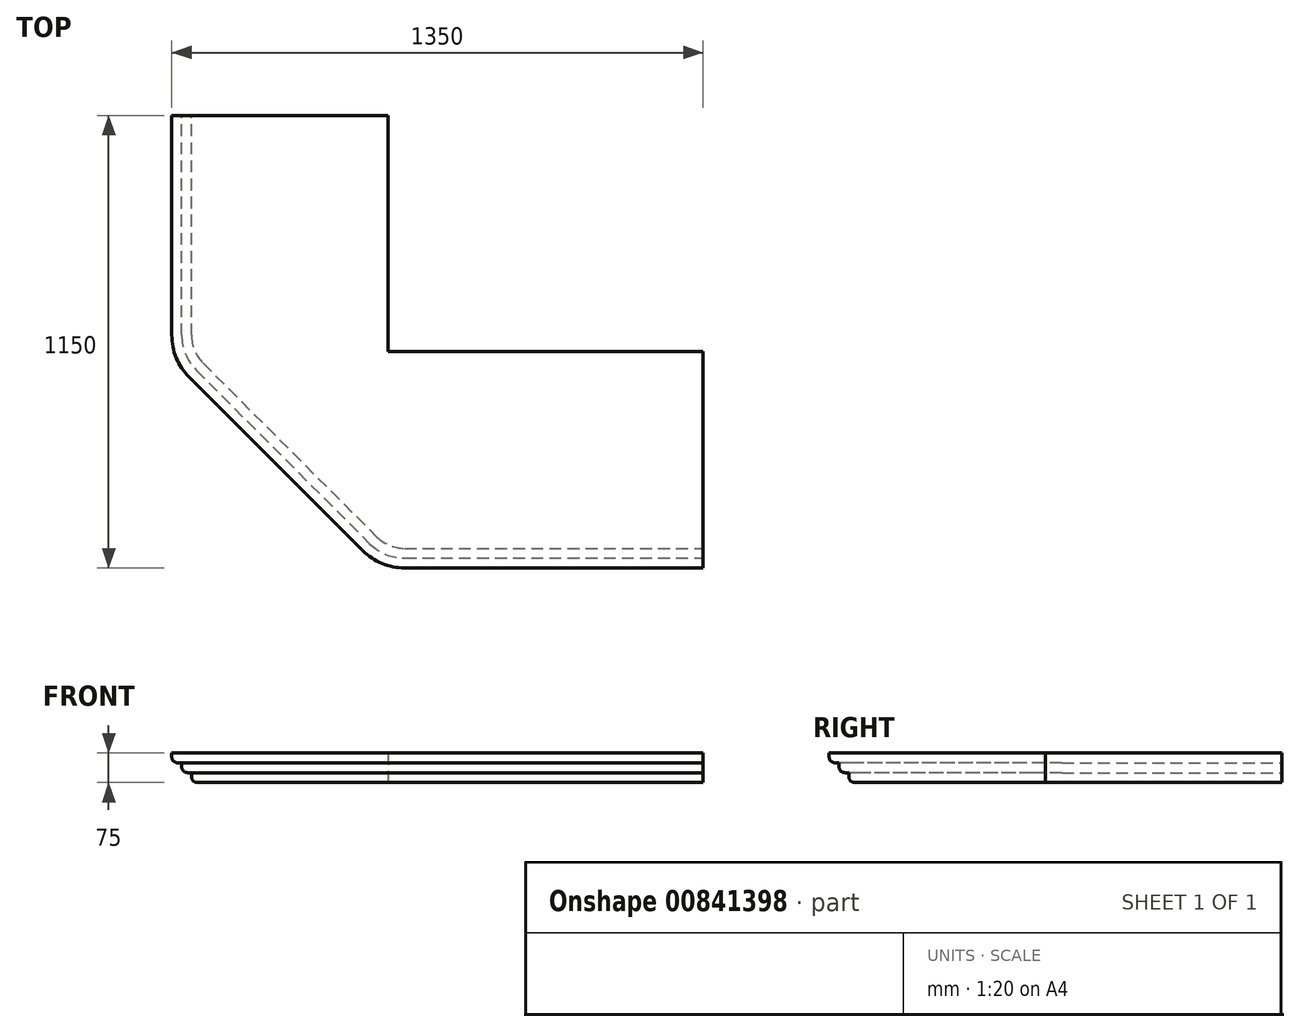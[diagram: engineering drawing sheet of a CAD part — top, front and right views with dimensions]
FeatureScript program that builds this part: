
annotation { "Feature Type Name" : "Feature", "Feature Type Description" : "" }
export const myFeature = defineFeature(function(context is Context, id is Id, definition is map)
    precondition{}
    {
        {
            var Q0;
            Q0=qCreatedBy(makeId("Top.planeOp"),FACE);
            var sketch = newSketch(context, id + "F0", { "sketchPlane" : qUnion([Q0])});
            skLineSegment(sketch, "E0.top", {"start": v(0, 600) * mm, "end": v(-500, 600) * mm});
            skLineSegment(sketch, "E0.left", {"start": v(0, 0) * mm, "end": v(0, 600) * mm});
            skLineSegment(sketch, "E0.right", {"start": v(-500, 0) * mm, "end": v(-500, 600) * mm});
            skLineSegment(sketch, "E1.bottom", {"start": v(0, 0) * mm, "end": v(800, 0) * mm});
            skLineSegment(sketch, "E1.top", {"start": v(0, -500) * mm, "end": v(800, -500) * mm});
            skLineSegment(sketch, "E1.right", {"start": v(800, 0) * mm, "end": v(800, -500) * mm});
            skLineSegment(sketch, "E2", {"start": v(-500, 0) * mm, "end": v(0, -500) * mm});
            skSolve(sketch);
        }
        {
            var Q0;
            Q0 = qSketchRegion(id + "F0", true);
            extrude(context, id + "F1", {"entities" : qUnion([Q0]), "depth" : 25 * mm, "offsetDistance" : 25 * mm});
        }
        {
            var Q0;
            Q0=makeQuery(id+"F1.opExtrude","SWEPT_EDGE",EDGE,{"disambiguationData":[OSD([sQuery(id+"F0.wireOp",EDGE,"E0.right"),sQuery(id+"F0.wireOp",EDGE,"E2")])]});
            var Q1;
            Q1=makeQuery(id+"F1.opExtrude","SWEPT_EDGE",EDGE,{"disambiguationData":[OSD([sQuery(id+"F0.wireOp",EDGE,"E1.top"),sQuery(id+"F0.wireOp",EDGE,"E2")])]});
            fillet(context, id + "F2", {"entities" : qUnion([Q0, Q1]), "radius" : 100 * mm, "tangentPropagation" : true, "allowEdgeOverflow" : false});
        }
        {
            var Q0;
            Q0=makeQuery(id+"F1.opExtrude","CAP_FACE",FACE,{"disambiguationData":[OSD([sQuery(id+"F0.wireOp",EDGE,"E0.top"),sQuery(id+"F0.wireOp",EDGE,"E0.left"),sQuery(id+"F0.wireOp",EDGE,"E0.right"),sQuery(id+"F0.wireOp",EDGE,"E1.bottom"),sQuery(id+"F0.wireOp",EDGE,"E1.top"),sQuery(id+"F0.wireOp",EDGE,"E1.right"),sQuery(id+"F0.wireOp",EDGE,"E2")])],"isStart":false});
            var sketch = newSketch(context, id + "F3", { "sketchPlane" : qUnion([Q0])});
            skArc(sketch, "E3.0", {"start": v(-525, 41.42) * mm, "mid": v(-515.48, -6.41) * mm, "end": v(-488.39, -46.97) * mm});
            skLineSegment(sketch, "E3.1", {"start": v(-488.39, -46.97) * mm, "end": v(-46.97, -488.39) * mm});
            skLineSegment(sketch, "E3.2", {"start": v(-525, 41.42) * mm, "end": v(-525, 625) * mm});
            skArc(sketch, "E3.3", {"start": v(-46.97, -488.39) * mm, "mid": v(-6.41, -515.48) * mm, "end": v(41.42, -525) * mm});
            skLineSegment(sketch, "E3.4", {"start": v(41.42, -525) * mm, "end": v(825, -525) * mm});
            skLineSegment(sketch, "E3.5", {"start": v(25, 625) * mm, "end": v(-525, 625) * mm});
            skLineSegment(sketch, "E3.6", {"start": v(25, 25) * mm, "end": v(25, 625) * mm});
            skLineSegment(sketch, "E3.7", {"start": v(25, 25) * mm, "end": v(825, 25) * mm});
            skLineSegment(sketch, "E3.8", {"start": v(825, 25) * mm, "end": v(825, -525) * mm});
            skSolve(sketch);
        }
        {
            var Q0;
            Q0 = qSketchRegion(id + "F3", true);
            extrude(context, id + "F4", {"entities" : qUnion([Q0]), "operationType" : NewBodyOperationType.ADD, "depth" : 25 * mm, "offsetDistance" : 25 * mm});
        }
        {
            var Q0;
            Q0=makeQuery(id+"F4.opExtrude","CAP_FACE",FACE,{"disambiguationData":[OSD([sQuery(id+"F3.wireOp",EDGE,"E3.0"),sQuery(id+"F3.wireOp",EDGE,"E3.1"),sQuery(id+"F3.wireOp",EDGE,"E3.2"),sQuery(id+"F3.wireOp",EDGE,"E3.3"),sQuery(id+"F3.wireOp",EDGE,"E3.4"),sQuery(id+"F3.wireOp",EDGE,"E3.5"),sQuery(id+"F3.wireOp",EDGE,"E3.6"),sQuery(id+"F3.wireOp",EDGE,"E3.7"),sQuery(id+"F3.wireOp",EDGE,"E3.8")])],"isStart":false});
            var sketch = newSketch(context, id + "F5", { "sketchPlane" : qUnion([Q0])});
            skArc(sketch, "E4.0", {"start": v(-550, 41.42) * mm, "mid": v(-538.58, -15.98) * mm, "end": v(-506.07, -64.64) * mm});
            skLineSegment(sketch, "E4.1", {"start": v(-506.07, -64.64) * mm, "end": v(-64.64, -506.07) * mm});
            skLineSegment(sketch, "E4.2", {"start": v(-550, 41.42) * mm, "end": v(-550, 650) * mm});
            skArc(sketch, "E4.3", {"start": v(-64.64, -506.07) * mm, "mid": v(-15.98, -538.58) * mm, "end": v(41.42, -550) * mm});
            skLineSegment(sketch, "E4.4", {"start": v(41.42, -550) * mm, "end": v(850, -550) * mm});
            skLineSegment(sketch, "E4.5", {"start": v(50, 650) * mm, "end": v(-550, 650) * mm});
            skLineSegment(sketch, "E4.6", {"start": v(50, 50) * mm, "end": v(50, 650) * mm});
            skLineSegment(sketch, "E4.7", {"start": v(50, 50) * mm, "end": v(850, 50) * mm});
            skLineSegment(sketch, "E4.8", {"start": v(850, 50) * mm, "end": v(850, -550) * mm});
            skSolve(sketch);
        }
        {
            var Q0;
            Q0 = qSketchRegion(id + "F5", true);
            extrude(context, id + "F6", {"entities" : qUnion([Q0]), "operationType" : NewBodyOperationType.ADD, "depth" : 25 * mm, "offsetDistance" : 25 * mm});
        }
        {
            var Q0;
            Q0=makeQuery(id+"F1.opExtrude","CAP_FACE",FACE,{"disambiguationData":[OSD([sQuery(id+"F0.wireOp",EDGE,"E0.top"),sQuery(id+"F0.wireOp",EDGE,"E0.left"),sQuery(id+"F0.wireOp",EDGE,"E0.right"),sQuery(id+"F0.wireOp",EDGE,"E1.bottom"),sQuery(id+"F0.wireOp",EDGE,"E1.top"),sQuery(id+"F0.wireOp",EDGE,"E1.right"),sQuery(id+"F0.wireOp",EDGE,"E2")])],"isStart":true});
            var sketch = newSketch(context, id + "F7", { "sketchPlane" : qUnion([Q0])});
            skLineSegment(sketch, "E5", {"start": v(800, 0) * mm, "end": v(800, 0) * mm});
            skLineSegment(sketch, "E6", {"start": v(800, 0) * mm, "end": v(0, 0) * mm});
            skLineSegment(sketch, "E7", {"start": v(0, 0) * mm, "end": v(0, -600) * mm});
            skLineSegment(sketch, "E8", {"start": v(0, -600) * mm, "end": v(-650.83, -600) * mm});
            skLineSegment(sketch, "E9", {"start": v(-650.83, -600) * mm, "end": v(-650.83, -840.36) * mm});
            skLineSegment(sketch, "E10", {"start": v(-650.83, -840.36) * mm, "end": v(869.27, -840.36) * mm});
            skLineSegment(sketch, "E11", {"start": v(869.27, -840.36) * mm, "end": v(869.27, 0) * mm});
            skLineSegment(sketch, "E12", {"start": v(800, 0) * mm, "end": v(800, 759.88) * mm});
            skLineSegment(sketch, "E13", {"start": v(800, 759.88) * mm, "end": v(869.27, 759.88) * mm});
            skLineSegment(sketch, "E14", {"start": v(869.27, 759.88) * mm, "end": v(869.27, 0) * mm});
            skSolve(sketch);
        }
        {
            var Q0;
            Q0 = qSketchRegion(id + "F7", true);
            extrude(context, id + "F8", {"entities" : qUnion([Q0]), "operationType" : NewBodyOperationType.REMOVE, "oppositeDirection" : true, "depth" : 539 * mm, "offsetDistance" : 25 * mm});
        }
        {
            var Q0;
            Q0=makeQuery(id+"F1.opExtrude","CAP_EDGE",EDGE,{"disambiguationData":[OSD([sQuery(id+"F0.wireOp",EDGE,"E1.top")])],"isStart":true});
            var Q1;
            Q1=makeQuery(id+"F4.opExtrude","CAP_EDGE",EDGE,{"disambiguationData":[OSD([sQuery(id+"F3.wireOp",EDGE,"E3.4")])],"isStart":true});
            var Q2;
            Q2=makeQuery(id+"F6.opExtrude","CAP_EDGE",EDGE,{"disambiguationData":[OSD([sQuery(id+"F5.wireOp",EDGE,"E4.4")])],"isStart":true});
            var Q3;
            {var subQ0=sQuery(id+"F0.wireOp",EDGE,"E2");var subQ1=sQuery(id+"F0.wireOp",EDGE,"E1.top");Q3=makeQuery(id+"F2.opFillet","BLEND_EDGE",EDGE,{"blendedFrom":[makeQuery(id+"F1.opExtrude","SWEPT_EDGE",EDGE,{"disambiguationData":[OSD([subQ1,subQ0])]}),makeQuery(id+"F1.opExtrude","CAP_FACE",FACE,{"disambiguationData":[OSD([sQuery(id+"F0.wireOp",EDGE,"E0.top"),sQuery(id+"F0.wireOp",EDGE,"E0.left"),sQuery(id+"F0.wireOp",EDGE,"E0.right"),sQuery(id+"F0.wireOp",EDGE,"E1.bottom"),subQ1,sQuery(id+"F0.wireOp",EDGE,"E1.right"),subQ0])],"isStart":true})],"blendedInto":[makeQuery(id+"F1.opExtrude","CAP_FACE",FACE,{"disambiguationData":[OSD([sQuery(id+"F0.wireOp",EDGE,"E0.top"),sQuery(id+"F0.wireOp",EDGE,"E0.left"),sQuery(id+"F0.wireOp",EDGE,"E0.right"),sQuery(id+"F0.wireOp",EDGE,"E1.bottom"),subQ1,sQuery(id+"F0.wireOp",EDGE,"E1.right"),subQ0])],"isStart":true})]});}
            var Q4;
            Q4=makeQuery(id+"F4.opExtrude","CAP_EDGE",EDGE,{"disambiguationData":[OSD([sQuery(id+"F3.wireOp",EDGE,"E3.3")])],"isStart":true});
            var Q5;
            Q5=makeQuery(id+"F6.opExtrude","CAP_EDGE",EDGE,{"disambiguationData":[OSD([sQuery(id+"F5.wireOp",EDGE,"E4.3")])],"isStart":true});
            var Q6;
            Q6=makeQuery(id+"F1.opExtrude","CAP_EDGE",EDGE,{"disambiguationData":[OSD([sQuery(id+"F0.wireOp",EDGE,"E2")])],"isStart":true});
            var Q7;
            Q7=makeQuery(id+"F4.opExtrude","CAP_EDGE",EDGE,{"disambiguationData":[OSD([sQuery(id+"F3.wireOp",EDGE,"E3.1")])],"isStart":true});
            var Q8;
            Q8=makeQuery(id+"F6.opExtrude","CAP_EDGE",EDGE,{"disambiguationData":[OSD([sQuery(id+"F5.wireOp",EDGE,"E4.1")])],"isStart":true});
            var Q9;
            {var subQ0=sQuery(id+"F0.wireOp",EDGE,"E2");var subQ1=sQuery(id+"F0.wireOp",EDGE,"E0.right");Q9=makeQuery(id+"F2.opFillet","BLEND_EDGE",EDGE,{"blendedFrom":[makeQuery(id+"F1.opExtrude","SWEPT_EDGE",EDGE,{"disambiguationData":[OSD([subQ1,subQ0])]}),makeQuery(id+"F1.opExtrude","CAP_FACE",FACE,{"disambiguationData":[OSD([sQuery(id+"F0.wireOp",EDGE,"E0.top"),sQuery(id+"F0.wireOp",EDGE,"E0.left"),subQ1,sQuery(id+"F0.wireOp",EDGE,"E1.bottom"),sQuery(id+"F0.wireOp",EDGE,"E1.top"),sQuery(id+"F0.wireOp",EDGE,"E1.right"),subQ0])],"isStart":true})],"blendedInto":[makeQuery(id+"F1.opExtrude","CAP_FACE",FACE,{"disambiguationData":[OSD([sQuery(id+"F0.wireOp",EDGE,"E0.top"),sQuery(id+"F0.wireOp",EDGE,"E0.left"),subQ1,sQuery(id+"F0.wireOp",EDGE,"E1.bottom"),sQuery(id+"F0.wireOp",EDGE,"E1.top"),sQuery(id+"F0.wireOp",EDGE,"E1.right"),subQ0])],"isStart":true})]});}
            var Q10;
            Q10=makeQuery(id+"F4.opExtrude","CAP_EDGE",EDGE,{"disambiguationData":[OSD([sQuery(id+"F3.wireOp",EDGE,"E3.0")])],"isStart":true});
            var Q11;
            Q11=makeQuery(id+"F6.opExtrude","CAP_EDGE",EDGE,{"disambiguationData":[OSD([sQuery(id+"F5.wireOp",EDGE,"E4.0")])],"isStart":true});
            var Q12;
            Q12=makeQuery(id+"F1.opExtrude","CAP_EDGE",EDGE,{"disambiguationData":[OSD([sQuery(id+"F0.wireOp",EDGE,"E0.right")])],"isStart":true});
            var Q13;
            Q13=makeQuery(id+"F4.opExtrude","CAP_EDGE",EDGE,{"disambiguationData":[OSD([sQuery(id+"F3.wireOp",EDGE,"E3.2")])],"isStart":true});
            var Q14;
            Q14=makeQuery(id+"F6.opExtrude","CAP_EDGE",EDGE,{"disambiguationData":[OSD([sQuery(id+"F5.wireOp",EDGE,"E4.2")])],"isStart":true});
            fillet(context, id + "F9", {"entities" : qUnion([Q0, Q1, Q2, Q3, Q4, Q5, Q6, Q7, Q8, Q9, Q10, Q11, Q12, Q13, Q14]), "radius" : 15 * mm, "tangentPropagation" : true, "allowEdgeOverflow" : false});
        }
    });
